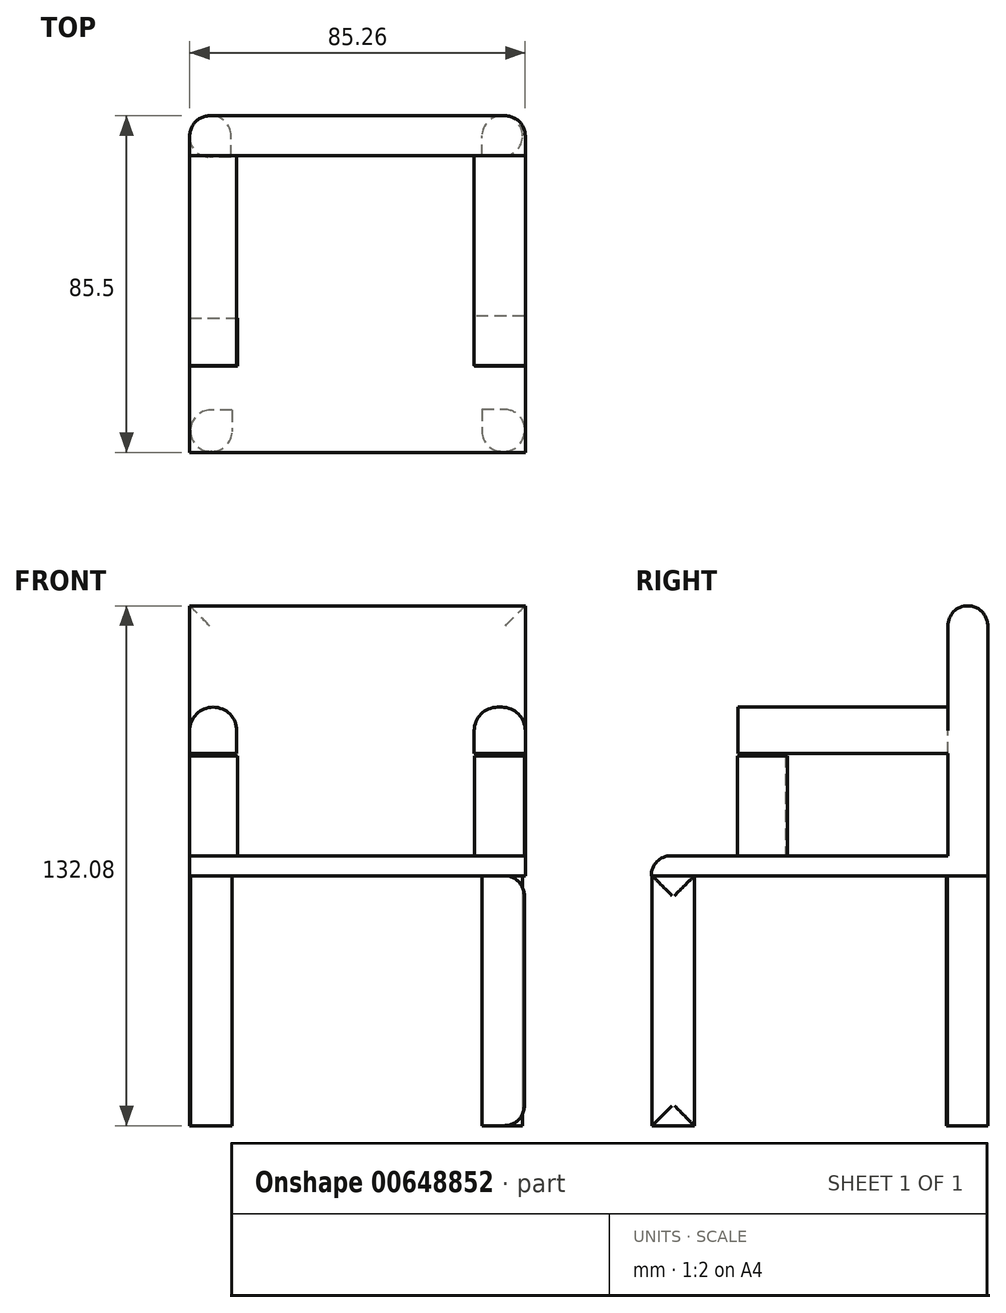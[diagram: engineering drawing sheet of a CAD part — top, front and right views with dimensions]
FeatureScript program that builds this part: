
annotation { "Feature Type Name" : "Feature", "Feature Type Description" : "" }
export const myFeature = defineFeature(function(context is Context, id is Id, definition is map)
    precondition{}
    {
        {
            var Q0;
            Q0=qCreatedBy(makeId("Top.planeOp"),FACE);
            var sketch = newSketch(context, id + "F0", { "sketchPlane" : qUnion([Q0])});
            skLineSegment(sketch, "E0.bottom", {"start": v(-31.77, 31.89) * mm, "end": v(-42.28, 31.89) * mm});
            skLineSegment(sketch, "E0.top", {"start": v(-31.77, 42.4) * mm, "end": v(-42.28, 42.4) * mm});
            skLineSegment(sketch, "E0.left", {"start": v(-31.77, 31.89) * mm, "end": v(-31.77, 42.4) * mm});
            skLineSegment(sketch, "E0.right", {"start": v(-42.28, 31.89) * mm, "end": v(-42.28, 42.4) * mm});
            skLineSegment(sketch, "E1.bottom", {"start": v(32, 32.12) * mm, "end": v(42.28, 32.12) * mm});
            skLineSegment(sketch, "E1.top", {"start": v(32, 42.4) * mm, "end": v(42.28, 42.4) * mm});
            skLineSegment(sketch, "E1.left", {"start": v(32, 32.12) * mm, "end": v(32, 42.4) * mm});
            skLineSegment(sketch, "E1.right", {"start": v(42.28, 32.12) * mm, "end": v(42.28, 42.4) * mm});
            skLineSegment(sketch, "E2.bottom", {"start": v(-31.54, -32.35) * mm, "end": v(-42.05, -32.35) * mm});
            skLineSegment(sketch, "E2.top", {"start": v(-31.54, -42.87) * mm, "end": v(-42.05, -42.87) * mm});
            skLineSegment(sketch, "E2.left", {"start": v(-31.54, -32.35) * mm, "end": v(-31.54, -42.87) * mm});
            skLineSegment(sketch, "E2.right", {"start": v(-42.05, -32.35) * mm, "end": v(-42.05, -42.87) * mm});
            skLineSegment(sketch, "E3.bottom", {"start": v(32, -32.12) * mm, "end": v(42.75, -32.12) * mm});
            skLineSegment(sketch, "E3.top", {"start": v(32, -42.87) * mm, "end": v(42.75, -42.87) * mm});
            skLineSegment(sketch, "E3.left", {"start": v(32, -32.12) * mm, "end": v(32, -42.87) * mm});
            skLineSegment(sketch, "E3.right", {"start": v(42.75, -32.12) * mm, "end": v(42.75, -42.87) * mm});
            skSolve(sketch);
        }
        {
            var Q0;
            Q0=qSketchRegion(id+"F0",true);
            extrude(context, id + "F1", {"entities" : qUnion([Q0]), "depth" : 63.5 * mm});
        }
        {
            var Q0;
            Q0=makeQuery(id+"F1.opExtrude","CAP_FACE",FACE,{"disambiguationData":[OSD([sQuery(id+"F0.wireOp",EDGE,"E0.bottom"),sQuery(id+"F0.wireOp",EDGE,"E0.top"),sQuery(id+"F0.wireOp",EDGE,"E0.left"),sQuery(id+"F0.wireOp",EDGE,"E0.right")])],"isStart":false});
            var sketch = newSketch(context, id + "F2", { "sketchPlane" : qUnion([Q0])});
            skLineSegment(sketch, "E4.bottom", {"start": v(-42.28, 42.4) * mm, "end": v(42.98, 42.4) * mm});
            skLineSegment(sketch, "E4.top", {"start": v(-42.28, -43.1) * mm, "end": v(42.98, -43.1) * mm});
            skLineSegment(sketch, "E4.left", {"start": v(-42.28, 42.4) * mm, "end": v(-42.28, -43.1) * mm});
            skLineSegment(sketch, "E4.right", {"start": v(42.98, 42.4) * mm, "end": v(42.98, -43.1) * mm});
            skSolve(sketch);
        }
        {
            var Q0;
            Q0=qSketchRegion(id+"F2",true);
            extrude(context, id + "F3", {"entities" : qUnion([Q0]), "depth" : 5.08 * mm});
        }
        {
            var Q0;
            Q0=makeQuery(id+"F3.opExtrude","CAP_FACE",FACE,{"disambiguationData":[OSD([sQuery(id+"F2.wireOp",EDGE,"E4.bottom"),sQuery(id+"F2.wireOp",EDGE,"E4.top"),sQuery(id+"F2.wireOp",EDGE,"E4.left"),sQuery(id+"F2.wireOp",EDGE,"E4.right")])],"isStart":false});
            var sketch = newSketch(context, id + "F4", { "sketchPlane" : qUnion([Q0])});
            skLineSegment(sketch, "E5.bottom", {"start": v(-42.28, 42.4) * mm, "end": v(42.98, 42.4) * mm});
            skLineSegment(sketch, "E5.top", {"start": v(-42.28, 32.24) * mm, "end": v(42.98, 32.24) * mm});
            skLineSegment(sketch, "E5.left", {"start": v(-42.28, 42.4) * mm, "end": v(-42.28, 32.24) * mm});
            skLineSegment(sketch, "E5.right", {"start": v(42.98, 42.4) * mm, "end": v(42.98, 32.24) * mm});
            skSolve(sketch);
        }
        {
            var Q0;
            Q0=qSketchRegion(id+"F4",true);
            extrude(context, id + "F5", {"entities" : qUnion([Q0]), "operationType" : NewBodyOperationType.ADD, "depth" : 63.5 * mm, "offsetDistance" : 25.4 * mm});
        }
        {
            var Q0;
            Q0=makeQuery(id+"F3.opExtrude","CAP_FACE",FACE,{"disambiguationData":[OSD([sQuery(id+"F2.wireOp",EDGE,"E4.bottom"),sQuery(id+"F2.wireOp",EDGE,"E4.top"),sQuery(id+"F2.wireOp",EDGE,"E4.left"),sQuery(id+"F2.wireOp",EDGE,"E4.right")])],"isStart":false});
            var sketch = newSketch(context, id + "F6", { "sketchPlane" : qUnion([Q0])});
            skLineSegment(sketch, "E6.bottom", {"start": v(-42.28, -8.67) * mm, "end": v(42.98, -8.67) * mm});
            skLineSegment(sketch, "E6.top", {"start": v(-42.28, -21.37) * mm, "end": v(42.98, -21.37) * mm});
            skLineSegment(sketch, "E6.left", {"start": v(-42.28, -8.67) * mm, "end": v(-42.28, -21.37) * mm});
            skLineSegment(sketch, "E6.right", {"start": v(42.98, -8.67) * mm, "end": v(42.98, -21.37) * mm});
            skSolve(sketch);
        }
        {
            var Q0;
            Q0=makeQuery(id+"F6.imprint","IMPRINT",FACE,{"disambiguationData":[TD([[makeQuery(id+"F6.imprint","IMPRINT",EDGE,{"derivedFrom":sQuery(id+"F6.wireOp",EDGE,"E6.bottom")}),-1.0]])]});
            var sketch = newSketch(context, id + "F7", { "sketchPlane" : qUnion([Q0])});
            skLineSegment(sketch, "E7.bottom", {"start": v(-42.28, -9) * mm, "end": v(-30.14, -9) * mm});
            skLineSegment(sketch, "E7.top", {"start": v(-42.28, -21.14) * mm, "end": v(-30.14, -21.14) * mm});
            skLineSegment(sketch, "E7.left", {"start": v(-42.28, -9) * mm, "end": v(-42.28, -21.14) * mm});
            skLineSegment(sketch, "E7.right", {"start": v(-30.14, -9) * mm, "end": v(-30.14, -21.14) * mm});
            skLineSegment(sketch, "E8.bottom", {"start": v(42.75, -8.52) * mm, "end": v(30.14, -8.52) * mm});
            skLineSegment(sketch, "E8.top", {"start": v(42.75, -21.14) * mm, "end": v(30.14, -21.14) * mm});
            skLineSegment(sketch, "E8.left", {"start": v(42.75, -8.52) * mm, "end": v(42.75, -21.14) * mm});
            skLineSegment(sketch, "E8.right", {"start": v(30.14, -8.52) * mm, "end": v(30.14, -21.14) * mm});
            skSolve(sketch);
        }
        {
            var Q0;
            Q0=qSketchRegion(id+"F7",true);
            extrude(context, id + "F8", {"entities" : qUnion([Q0]), "operationType" : NewBodyOperationType.ADD, "depth" : 25.4 * mm, "offsetDistance" : 25.4 * mm});
        }
        {
            var Q0;
            Q0=makeQuery(id+"F5.opExtrude","SWEPT_FACE",FACE,{"disambiguationData":[OSD([sQuery(id+"F4.wireOp",EDGE,"E5.top")])]});
            var sketch = newSketch(context, id + "F9", { "sketchPlane" : qUnion([Q0])});
            skLineSegment(sketch, "E9.bottom", {"start": v(-42.28, 94.5) * mm, "end": v(-30.33, 94.5) * mm});
            skLineSegment(sketch, "E9.top", {"start": v(-42.28, 106.32) * mm, "end": v(-30.33, 106.32) * mm});
            skLineSegment(sketch, "E9.left", {"start": v(-42.28, 94.5) * mm, "end": v(-42.28, 106.32) * mm});
            skLineSegment(sketch, "E9.right", {"start": v(-30.33, 94.5) * mm, "end": v(-30.33, 106.32) * mm});
            skLineSegment(sketch, "E10.bottom", {"start": v(42.98, 94.5) * mm, "end": v(30.01, 94.5) * mm});
            skLineSegment(sketch, "E10.top", {"start": v(42.98, 106.32) * mm, "end": v(30.01, 106.32) * mm});
            skLineSegment(sketch, "E10.left", {"start": v(42.98, 94.5) * mm, "end": v(42.98, 106.32) * mm});
            skLineSegment(sketch, "E10.right", {"start": v(30.01, 94.5) * mm, "end": v(30.01, 106.32) * mm});
            skSolve(sketch);
        }
        {
            var Q0;
            Q0=qSketchRegion(id+"F9",true);
            extrude(context, id + "F10", {"entities" : qUnion([Q0]), "operationType" : NewBodyOperationType.ADD, "depth" : 53.34 * mm, "offsetDistance" : 25.4 * mm});
        }
        {
            var Q0;
            Q0=makeQuery(id+"F3.opExtrude","CAP_EDGE",EDGE,{"disambiguationData":[OSD([sQuery(id+"F2.wireOp",EDGE,"E4.top")])],"isStart":false});
            var Q1;
            Q1=makeQuery(id+"F5.opExtrude","CAP_EDGE",EDGE,{"disambiguationData":[OSD([sQuery(id+"F4.wireOp",EDGE,"E5.top")])],"isStart":false});
            var Q2;
            Q2=makeQuery(id+"F5.opExtrude","CAP_EDGE",EDGE,{"disambiguationData":[OSD([sQuery(id+"F4.wireOp",EDGE,"E5.bottom")])],"isStart":false});
            var Q3;
            Q3=makeQuery(id+"F5.boolean.opBoolean","MERGE",EDGE,{"derivedFrom":[makeQuery(id+"F3.opExtrude","SWEPT_EDGE",EDGE,{"disambiguationData":[OSD([sQuery(id+"F2.wireOp",EDGE,"E4.bottom"),sQuery(id+"F2.wireOp",EDGE,"E4.right")])]}),makeQuery(id+"F5.opExtrude","SWEPT_EDGE",EDGE,{"disambiguationData":[OSD([sQuery(id+"F4.wireOp",EDGE,"E5.bottom"),sQuery(id+"F4.wireOp",EDGE,"E5.right")])]})]});
            var Q4;
            Q4=makeQuery(id+"F5.boolean.opBoolean","MERGE",EDGE,{"derivedFrom":[makeQuery(id+"F3.opExtrude","SWEPT_EDGE",EDGE,{"disambiguationData":[OSD([sQuery(id+"F2.wireOp",EDGE,"E4.bottom"),sQuery(id+"F2.wireOp",EDGE,"E4.left")])]}),makeQuery(id+"F5.opExtrude","SWEPT_EDGE",EDGE,{"disambiguationData":[OSD([sQuery(id+"F4.wireOp",EDGE,"E5.bottom"),sQuery(id+"F4.wireOp",EDGE,"E5.left")])]})]});
            var Q5;
            Q5=makeQuery(id+"F1.opExtrude","SWEPT_EDGE",EDGE,{"disambiguationData":[OSD([sQuery(id+"F0.wireOp",EDGE,"E0.top"),sQuery(id+"F0.wireOp",EDGE,"E0.right")])]});
            var Q6;
            Q6=makeQuery(id+"F1.opExtrude","SWEPT_EDGE",EDGE,{"disambiguationData":[OSD([sQuery(id+"F0.wireOp",EDGE,"E0.bottom"),sQuery(id+"F0.wireOp",EDGE,"E0.right")])]});
            var Q7;
            Q7=makeQuery(id+"F1.opExtrude","SWEPT_EDGE",EDGE,{"disambiguationData":[OSD([sQuery(id+"F0.wireOp",EDGE,"E2.top"),sQuery(id+"F0.wireOp",EDGE,"E2.right")])]});
            var Q8;
            Q8=makeQuery(id+"F1.opExtrude","SWEPT_EDGE",EDGE,{"disambiguationData":[OSD([sQuery(id+"F0.wireOp",EDGE,"E2.bottom"),sQuery(id+"F0.wireOp",EDGE,"E2.right")])]});
            var Q9;
            Q9=makeQuery(id+"F1.opExtrude","SWEPT_EDGE",EDGE,{"disambiguationData":[OSD([sQuery(id+"F0.wireOp",EDGE,"E2.top"),sQuery(id+"F0.wireOp",EDGE,"E2.left")])]});
            var Q10;
            Q10=makeQuery(id+"F1.opExtrude","SWEPT_EDGE",EDGE,{"disambiguationData":[OSD([sQuery(id+"F0.wireOp",EDGE,"E3.top"),sQuery(id+"F0.wireOp",EDGE,"E3.left")])]});
            var Q11;
            Q11=makeQuery(id+"F1.opExtrude","SWEPT_EDGE",EDGE,{"disambiguationData":[OSD([sQuery(id+"F0.wireOp",EDGE,"E3.top"),sQuery(id+"F0.wireOp",EDGE,"E3.right")])]});
            var Q12;
            Q12=makeQuery(id+"F1.opExtrude","SWEPT_FACE",FACE,{"disambiguationData":[OSD([sQuery(id+"F0.wireOp",EDGE,"E3.right")])]});
            var Q13;
            Q13=makeQuery(id+"F1.opExtrude","SWEPT_EDGE",EDGE,{"disambiguationData":[OSD([sQuery(id+"F0.wireOp",EDGE,"E1.top"),sQuery(id+"F0.wireOp",EDGE,"E1.right")])]});
            var Q14;
            Q14=makeQuery(id+"F1.opExtrude","SWEPT_EDGE",EDGE,{"disambiguationData":[OSD([sQuery(id+"F0.wireOp",EDGE,"E1.bottom"),sQuery(id+"F0.wireOp",EDGE,"E1.right")])]});
            var Q15;
            Q15=makeQuery(id+"F1.opExtrude","SWEPT_EDGE",EDGE,{"disambiguationData":[OSD([sQuery(id+"F0.wireOp",EDGE,"E1.top"),sQuery(id+"F0.wireOp",EDGE,"E1.left")])]});
            fillet(context, id + "F11", {"entities" : qUnion([Q0, Q1, Q2, Q3, Q4, Q5, Q6, Q7, Q8, Q9, Q10, Q11, Q12, Q13, Q14, Q15]), "radius" : 5.08 * mm, "tangentPropagation" : true, "allowEdgeOverflow" : false});
        }
        {
            var Q0;
            {var subQ0=sQuery(id+"F0.wireOp",EDGE,"E1.left");Q0=makeQuery(id+"F11.opFillet","BLEND_EDGE",EDGE,{"blendedFrom":[makeQuery(id+"F1.opExtrude","SWEPT_EDGE",EDGE,{"disambiguationData":[OSD([sQuery(id+"F0.wireOp",EDGE,"E1.top"),subQ0])]}),makeQuery(id+"F1.opExtrude","SWEPT_FACE",FACE,{"disambiguationData":[OSD([subQ0])]})],"blendedInto":[makeQuery(id+"F1.opExtrude","SWEPT_FACE",FACE,{"disambiguationData":[OSD([subQ0])]})]});}
            var Q1;
            Q1=makeQuery(id+"F1.opExtrude","SWEPT_EDGE",EDGE,{"disambiguationData":[OSD([sQuery(id+"F0.wireOp",EDGE,"E0.top"),sQuery(id+"F0.wireOp",EDGE,"E0.left")])]});
            var Q2;
            {var subQ0=sQuery(id+"F0.wireOp",EDGE,"E0.top");Q2=makeQuery(id+"F11.opFillet","BLEND_EDGE",EDGE,{"blendedFrom":[makeQuery(id+"F1.opExtrude","SWEPT_EDGE",EDGE,{"disambiguationData":[OSD([subQ0,sQuery(id+"F0.wireOp",EDGE,"E0.right")])]}),makeQuery(id+"F1.opExtrude","SWEPT_FACE",FACE,{"disambiguationData":[OSD([subQ0])]})],"blendedInto":[makeQuery(id+"F1.opExtrude","SWEPT_FACE",FACE,{"disambiguationData":[OSD([subQ0])]})]});}
            var Q3;
            {var subQ0=sQuery(id+"F0.wireOp",EDGE,"E0.right");Q3=makeQuery(id+"F11.opFillet","BLEND_EDGE",EDGE,{"blendedFrom":[makeQuery(id+"F1.opExtrude","SWEPT_EDGE",EDGE,{"disambiguationData":[OSD([sQuery(id+"F0.wireOp",EDGE,"E0.top"),subQ0])]}),makeQuery(id+"F1.opExtrude","SWEPT_FACE",FACE,{"disambiguationData":[OSD([subQ0])]})],"blendedInto":[makeQuery(id+"F1.opExtrude","SWEPT_FACE",FACE,{"disambiguationData":[OSD([subQ0])]})]});}
            fillet(context, id + "F12", {"entities" : qUnion([Q0, Q1, Q2, Q3]), "radius" : 5.08 * mm, "tangentPropagation" : true, "allowEdgeOverflow" : false});
        }
        {
            var Q0;
            Q0=makeQuery(id+"F10.opExtrude","SWEPT_EDGE",EDGE,{"disambiguationData":[OSD([sQuery(id+"F2.wireOp",EDGE,"E4.left"),sQuery(id+"F4.wireOp",EDGE,"E5.top"),sQuery(id+"F4.wireOp",EDGE,"E5.left"),sQuery(id+"F9.wireOp",EDGE,"E9.top"),sQuery(id+"F9.wireOp",EDGE,"E9.left")])]});
            var Q1;
            Q1=makeQuery(id+"F10.opExtrude","SWEPT_EDGE",EDGE,{"disambiguationData":[OSD([sQuery(id+"F9.wireOp",EDGE,"E9.top"),sQuery(id+"F9.wireOp",EDGE,"E9.right")])]});
            var Q2;
            Q2=makeQuery(id+"F10.opExtrude","SWEPT_EDGE",EDGE,{"disambiguationData":[OSD([sQuery(id+"F9.wireOp",EDGE,"E10.top"),sQuery(id+"F9.wireOp",EDGE,"E10.right")])]});
            var Q3;
            Q3=makeQuery(id+"F10.opExtrude","SWEPT_EDGE",EDGE,{"disambiguationData":[OSD([sQuery(id+"F2.wireOp",EDGE,"E4.right"),sQuery(id+"F4.wireOp",EDGE,"E5.top"),sQuery(id+"F4.wireOp",EDGE,"E5.right"),sQuery(id+"F9.wireOp",EDGE,"E10.top"),sQuery(id+"F9.wireOp",EDGE,"E10.left")])]});
            fillet(context, id + "F13", {"entities" : qUnion([Q0, Q1, Q2, Q3]), "radius" : 5.97 * mm, "tangentPropagation" : true, "allowEdgeOverflow" : false});
        }
    });
